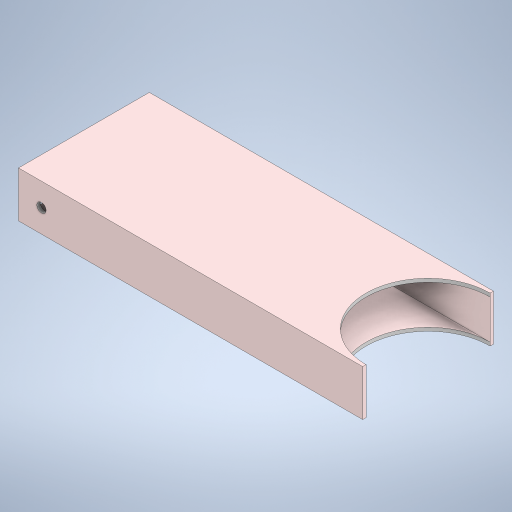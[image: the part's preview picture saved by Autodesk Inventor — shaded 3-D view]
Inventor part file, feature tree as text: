
AUTODESK INVENTOR PART (.ipt)
format: ipt  version: 2024.3 (Build 283343000, 343)  size: 253,952 bytes
history: native  units: mm
features: extrude x3, sketch x3
ambient origin geometry x8: Origin, YZ Plane, XZ Plane, XY Plane, X Axis, Y Axis, Z Axis, Center Point
bodies: Solid1 (feature_tree)
feature tree (6):
  extrude  "Extrusion1"  Depth=40.0mm
  extrude  "Extrusion2"  Depth=3.0mm
  extrude  "Extrusion3"  TaperAngle=0.0deg  [1 undecoded]
  sketch  "Sketch1"  dims[d0=114.0mm d1=40.0mm]
  sketch  "Sketch2"  dims[d2=3.0mm d3=3.0mm]
  sketch  "Sketch3"  dims[d4=300.0mm d5=0.0mm d6=0.0mm d7=0.0mm d8=8.0mm d9=20.0mm d10=10.0mm d11=0.0mm]
note: 1 required parameter value undecoded (feature->parameter linkage not recoverable at this tier; creation-order binding heuristic only, values carry confidence <= 0.55)
